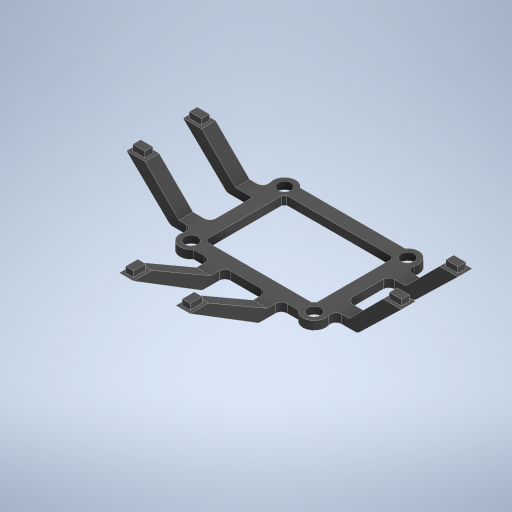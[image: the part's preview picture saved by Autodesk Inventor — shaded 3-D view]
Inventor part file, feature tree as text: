
AUTODESK INVENTOR PART (.ipt)
format: ipt  version: 2024.2 (Build 282272000, 272)  size: 474,112 bytes
history: native  units: mm
features: extrude x5, mirror x5, sketch x5, plane x4, fillet x2, chamfer x1
ambient origin geometry x8: Origin, YZ Plane, XZ Plane, XY Plane, X Axis, Y Axis, Z Axis, Center Point
bodies: Solid1 (feature_tree)
feature tree (22):
  extrude  "Extrusion1"  Depth=8.0mm
  chamfer  "Chamfer1"  Distance=4.7mm
  plane  "Work Plane2"
  extrude  "Extrusion2"  Depth=8.0mm
  plane  "Work Plane4"
  plane  "Work Plane5"
  mirror  "Mirror1"
  mirror  "Mirror2"
  plane  "Work Plane6"
  extrude  "Extrusion5"  Depth=4.0mm
  mirror  "Mirror5"
  extrude  "Extrusion4"  Depth=4.0mm
  mirror  "Mirror3"
  mirror  "Mirror4"
  extrude  "Extrusion6"  Depth=4.0mm
  fillet  "Fillet1"  Radius=4.0mm
  fillet  "Fillet2"  Radius=4.0mm
  sketch  "Sketch1"  dims[d0=4.7mm d1=8.0mm]
  sketch  "Sketch2"  dims[d2=4.7mm]
  sketch  "Sketch5"  dims[d3=8.0mm]
  sketch  "Sketch7"  dims[d4=4.7mm]
  sketch  "Sketch8"  dims[d5=8.0mm d6=4.7mm d7=8.0mm d8=4.0mm d9=4.0mm d10=4.0mm d11=4.0mm d12=4.0mm d13=4.0mm d14=4.0mm d15=4.0mm d16=33.0mm d17=4.7mm d18=4.7mm d19=4.7mm d20=4.7mm d21=2.35mm d22=2.35mm d23=2.35mm d24=2.35mm d25=43.5mm d26=3.0mm d27=0.0mm d28=0.5mm d29=2.0mm d30=45.0deg d32=4.0mm d41=5.0mm d42=0.0mm d47=21.75mm d48=16.5mm d49=6.5mm d61=9.0mm d62=4.3mm d63=2.8mm d64=1.1mm d65=1.1mm d66=2.0mm d67=0.0mm d71=9.25mm d72=8.0mm d73=6.5mm d76=5.0mm d77=0.0mm d78=2.8mm d79=4.3mm d80=2.8mm d81=4.3mm d82=1.1mm d83=1.1mm d84=1.1mm d85=1.1mm d86=2.0mm d87=0.0mm d91=6.0mm d93=45.0deg d94=15.0mm d95=15.0mm d96=2.0mm d97=2.0mm d98=5.0mm d99=30.0deg]
